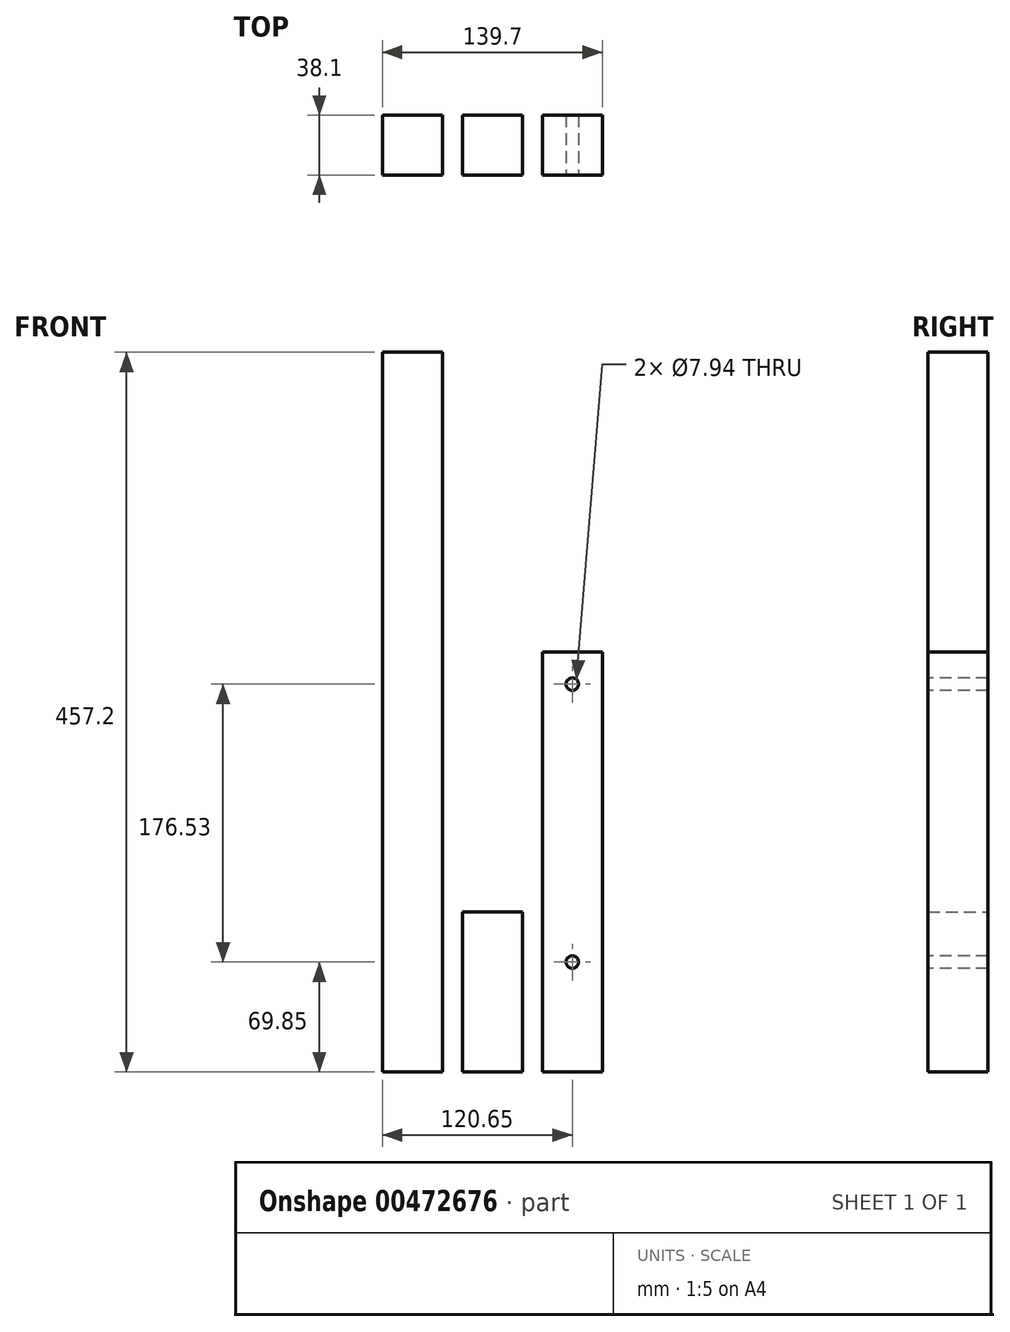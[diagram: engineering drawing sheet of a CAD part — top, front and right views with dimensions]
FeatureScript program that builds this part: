
annotation { "Feature Type Name" : "Feature", "Feature Type Description" : "" }
export const myFeature = defineFeature(function(context is Context, id is Id, definition is map)
    precondition{}
    {
        {
            var Q0;
            Q0=qCreatedBy(makeId("Top.planeOp"),FACE);
            var sketch = newSketch(context, id + "F0", { "sketchPlane" : qUnion([Q0])});
            skLineSegment(sketch, "E0.bottom", {"start": v(0, 0) * mm, "end": v(38.1, 0) * mm});
            skLineSegment(sketch, "E0.top", {"start": v(0, 38.1) * mm, "end": v(38.1, 38.1) * mm});
            skLineSegment(sketch, "E0.left", {"start": v(0, 0) * mm, "end": v(0, 38.1) * mm});
            skLineSegment(sketch, "E0.right", {"start": v(38.1, 0) * mm, "end": v(38.1, 38.1) * mm});
            skLineSegment(sketch, "E1.1.0.0", {"start": v(50.8, 38.1) * mm, "end": v(88.9, 38.1) * mm});
            skLineSegment(sketch, "E1.1.0.1", {"start": v(50.8, 0) * mm, "end": v(50.8, 38.1) * mm});
            skLineSegment(sketch, "E1.1.0.2", {"start": v(50.8, 0) * mm, "end": v(88.9, 0) * mm});
            skLineSegment(sketch, "E1.1.0.3", {"start": v(88.9, 0) * mm, "end": v(88.9, 38.1) * mm});
            skLineSegment(sketch, "E1.2.0.0", {"start": v(101.6, 38.1) * mm, "end": v(139.7, 38.1) * mm});
            skLineSegment(sketch, "E1.2.0.1", {"start": v(101.6, 0) * mm, "end": v(101.6, 38.1) * mm});
            skLineSegment(sketch, "E1.2.0.2", {"start": v(101.6, 0) * mm, "end": v(139.7, 0) * mm});
            skLineSegment(sketch, "E1.2.0.3", {"start": v(139.7, 0) * mm, "end": v(139.7, 38.1) * mm});
            skLineSegment(sketch, "E1.direction1", {"start": v(0, 38.1) * mm, "end": v(50.8, 38.1) * mm, "construction": true});
            skSolve(sketch);
        }
        {
            var Q0;
            Q0=makeQuery(id+"F0.imprint","IMPRINT",FACE,{"disambiguationData":[TD([[makeQuery(id+"F0.imprint","IMPRINT",EDGE,{"derivedFrom":sQuery(id+"F0.wireOp",EDGE,"E0.bottom")}),1.0]])]});
            extrude(context, id + "F1", {"entities" : qUnion([Q0]), "depth" : 457.2 * mm, "offsetDistance" : 25.4 * mm});
        }
        {
            var Q0;
            Q0=makeQuery(id+"F0.imprint","IMPRINT",FACE,{"disambiguationData":[TD([[makeQuery(id+"F0.imprint","IMPRINT",EDGE,{"derivedFrom":sQuery(id+"F0.wireOp",EDGE,"E1.1.0.0")}),-1.0]])]});
            extrude(context, id + "F2", {"entities" : qUnion([Q0]), "depth" : 101.6 * mm, "offsetDistance" : 25.4 * mm});
        }
        {
            var Q0;
            Q0=makeQuery(id+"F0.imprint","IMPRINT",FACE,{"disambiguationData":[TD([[makeQuery(id+"F0.imprint","IMPRINT",EDGE,{"derivedFrom":sQuery(id+"F0.wireOp",EDGE,"E1.2.0.0")}),-1.0]])]});
            extrude(context, id + "F3", {"entities" : qUnion([Q0]), "depth" : 266.7 * mm, "offsetDistance" : 25.4 * mm});
        }
        {
            var Q0;
            Q0=makeQuery(id+"F3.opExtrude","SWEPT_FACE",FACE,{"disambiguationData":[OSD([sQuery(id+"F0.wireOp",EDGE,"E1.2.0.2")])]});
            var sketch = newSketch(context, id + "F4", { "sketchPlane" : qUnion([Q0])});
            skCircle(sketch, "E2", {"center": v(120.65, 69.85) * mm, "radius": 3.97 * mm});
            skCircle(sketch, "E3", {"center": v(120.65, 246.38) * mm, "radius": 3.97 * mm});
            skLineSegment(sketch, "E4", {"start": v(120.65, 0) * mm, "end": v(120.65, 266.7) * mm, "construction": true});
            skSolve(sketch);
        }
        {
            var Q0;
            Q0 = qSketchRegion(id + "F4", true);
            extrude(context, id + "F5", {"entities" : qUnion([Q0]), "operationType" : NewBodyOperationType.REMOVE, "endBound" : BoundingType.THROUGH_ALL, "oppositeDirection" : true, "depth" : 25.4 * mm, "offsetDistance" : 25.4 * mm});
        }
    });
